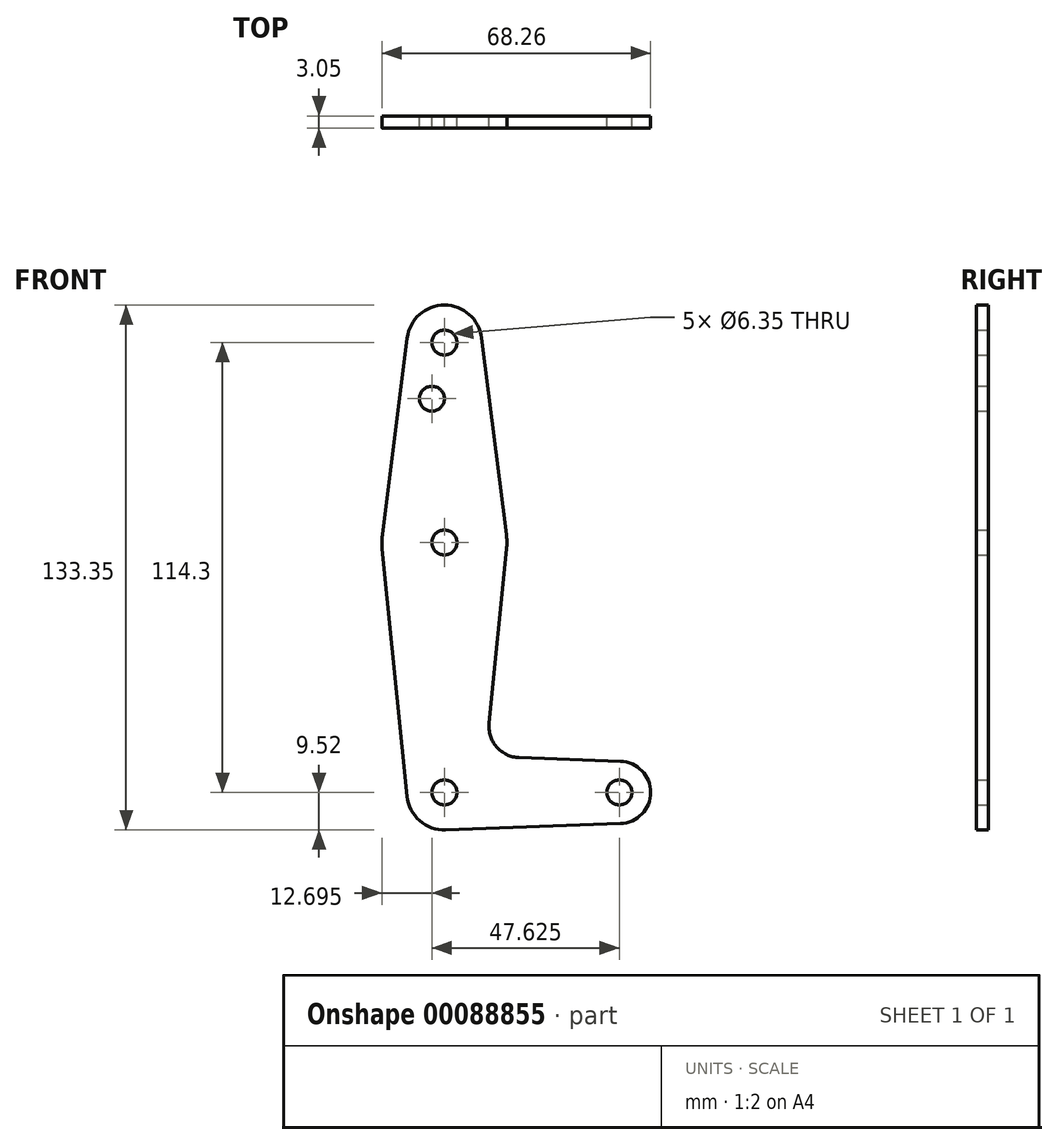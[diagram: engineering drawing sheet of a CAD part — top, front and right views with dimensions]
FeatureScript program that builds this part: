
annotation { "Feature Type Name" : "Feature", "Feature Type Description" : "" }
export const myFeature = defineFeature(function(context is Context, id is Id, definition is map)
    precondition{}
    {
        {
            var Q0;
            Q0=qCreatedBy(makeId("Front.planeOp"),FACE);
            var sketch = newSketch(context, id + "F0", { "sketchPlane" : qUnion([Q0])});
            skLineSegment(sketch, "E0", {"start": v(0, 0) * mm, "end": v(0, 114.3) * mm, "construction": true});
            skCircle(sketch, "E1", {"center": v(0, 114.3) * mm, "radius": 9.53 * mm});
            skCircle(sketch, "E2", {"center": v(0, 63.5) * mm, "radius": 15.88 * mm});
            skCircle(sketch, "E3", {"center": v(0, 0) * mm, "radius": 9.53 * mm});
            skCircle(sketch, "E4", {"center": v(44.45, 0) * mm, "radius": 7.94 * mm});
            skLineSegment(sketch, "E5", {"start": v(18.97, 8.85) * mm, "end": v(44.73, 7.93) * mm});
            skLineSegment(sketch, "E6", {"start": v(15.8, 61.91) * mm, "end": v(11.34, 17.6) * mm});
            skCircle(sketch, "E7", {"center": v(-3.18, 100.03) * mm, "radius": 3.18 * mm});
            skArc(sketch, "E8.filletArc", {"start": v(11.34, 17.6) * mm, "mid": v(13.26, 11.57) * mm, "end": v(18.97, 8.85) * mm});
            skLineSegment(sketch, "E9", {"start": v(0.34, -9.52) * mm, "end": v(44.73, -7.93) * mm});
            skCircle(sketch, "E10", {"center": v(0, 114.3) * mm, "radius": 3.18 * mm});
            skCircle(sketch, "E11", {"center": v(0, 63.5) * mm, "radius": 3.18 * mm});
            skCircle(sketch, "E12", {"center": v(0, 0) * mm, "radius": 3.18 * mm});
            skLineSegment(sketch, "E13", {"start": v(0, 0) * mm, "end": v(44.45, 0) * mm});
            skCircle(sketch, "E14", {"center": v(44.45, 0) * mm, "radius": 3.18 * mm});
            skLineSegment(sketch, "E15", {"start": v(-15.8, 61.91) * mm, "end": v(-9.48, -0.95) * mm});
            skLineSegment(sketch, "E16", {"start": v(-9.45, 115.5) * mm, "end": v(-15.75, 65.48) * mm});
            skLineSegment(sketch, "E17", {"start": v(9.45, 115.5) * mm, "end": v(15.75, 65.48) * mm});
            skSolve(sketch);
        }
        {
            var Q0;
            Q0 = qSketchRegion(id + "F0", true);
            extrude(context, id + "F1", {"entities" : qUnion([Q0]), "depth" : 3.05 * mm});
        }
    });
